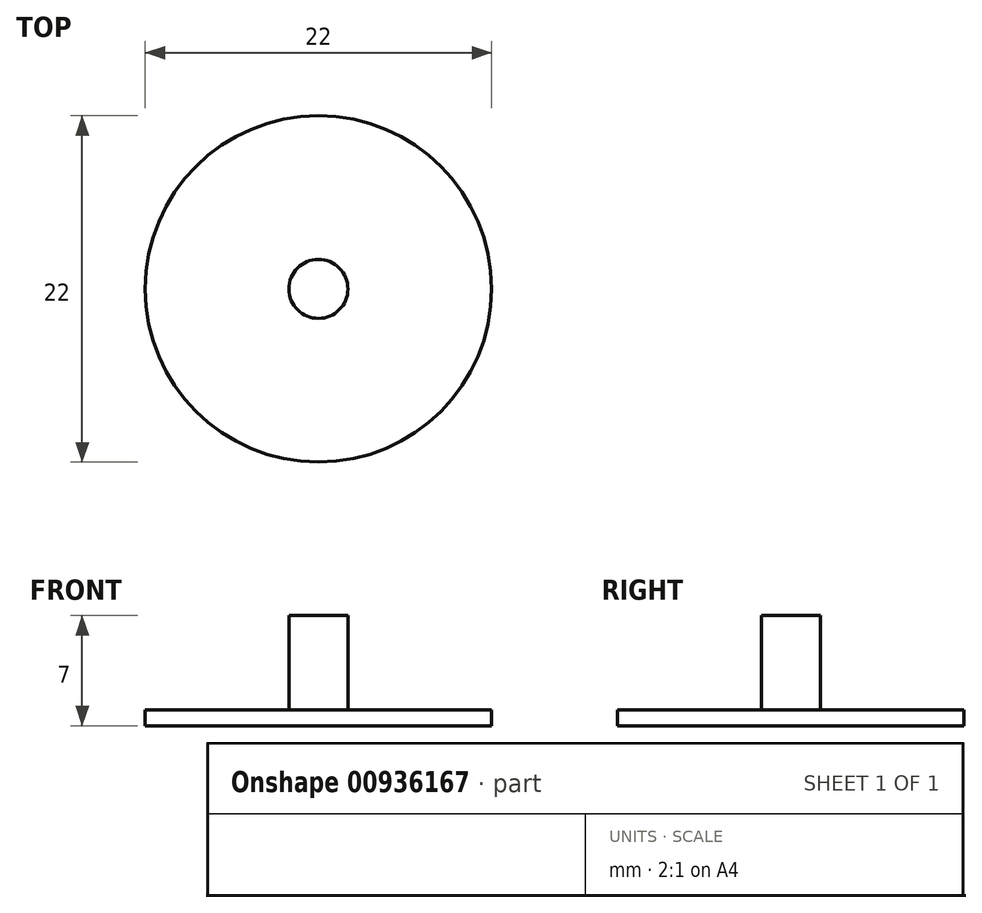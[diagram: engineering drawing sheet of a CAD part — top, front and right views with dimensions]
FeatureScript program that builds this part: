
annotation { "Feature Type Name" : "Feature", "Feature Type Description" : "" }
export const myFeature = defineFeature(function(context is Context, id is Id, definition is map)
    precondition{}
    {
        {
            var Q0;
            Q0=qCreatedBy(makeId("Top.planeOp"),FACE);
            var sketch = newSketch(context, id + "F0", { "sketchPlane" : qUnion([Q0])});
            skCircle(sketch, "E0", {"center": v(0, 0) * mm, "radius": 11 * mm});
            skSolve(sketch);
        }
        {
            var Q0;
            Q0=makeQuery(id+"F0.imprint","IMPRINT",FACE,{"disambiguationData":[TD([[makeQuery(id+"F0.imprint","IMPRINT",EDGE,{"derivedFrom":sQuery(id+"F0.wireOp",EDGE,"E0")}),1.0]])]});
            extrude(context, id + "F1", {"entities" : qUnion([Q0]), "depth" : 1 * mm, "offsetDistance" : 25.4 * mm});
        }
        {
            var Q0;
            Q0=makeQuery(id+"F1.opExtrude","CAP_FACE",FACE,{"disambiguationData":[OSD([sQuery(id+"F0.wireOp",EDGE,"E0")])],"isStart":false});
            var Q1;
            Q1=makeQuery(id+"F1.opExtrude","CAP_FACE",FACE,{"disambiguationData":[OSD([sQuery(id+"F0.wireOp",EDGE,"E0")])],"isStart":false});
            var sketch = newSketch(context, id + "F2", { "sketchPlane" : qUnion([Q0, Q1])});
            skCircle(sketch, "E1", {"center": v(0, 0) * mm, "radius": 1.88 * mm});
            skSolve(sketch);
        }
        {
            var Q0;
            Q0 = qSketchRegion(id + "F2", true);
            extrude(context, id + "F3", {"entities" : qUnion([Q0]), "operationType" : NewBodyOperationType.ADD, "depth" : 6 * mm, "offsetDistance" : 25.4 * mm});
        }
    });
